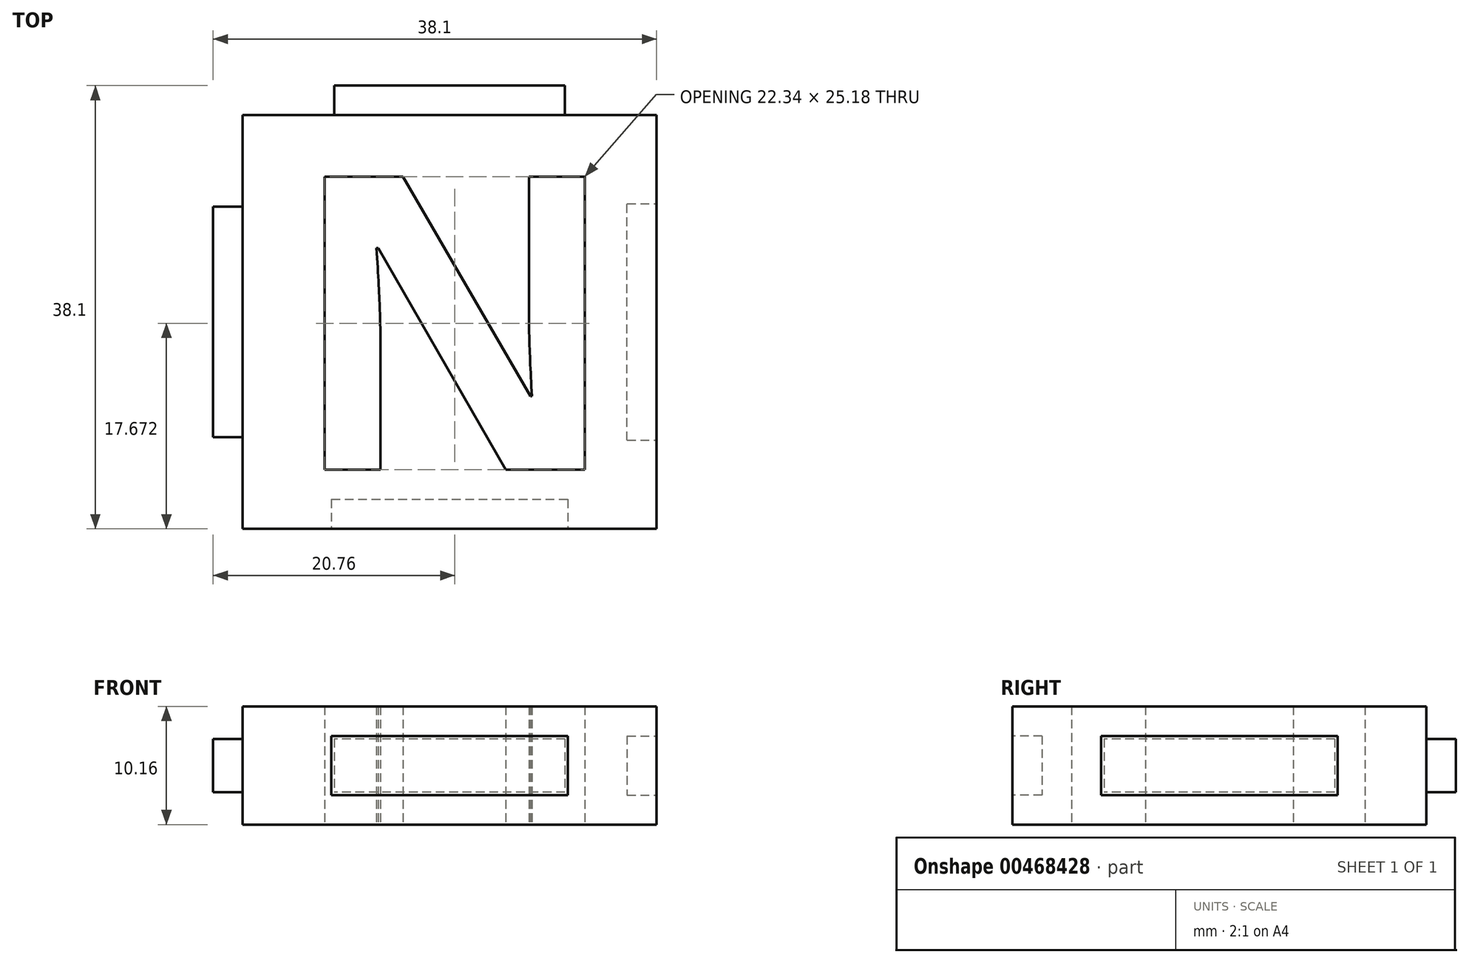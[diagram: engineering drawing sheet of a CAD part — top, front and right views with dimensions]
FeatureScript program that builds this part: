
annotation { "Feature Type Name" : "Feature", "Feature Type Description" : "" }
export const myFeature = defineFeature(function(context is Context, id is Id, definition is map)
    precondition{}
    {
        {
            var Q0;
            Q0=qCreatedBy(makeId("Top.planeOp"),FACE);
            var sketch = newSketch(context, id + "F0", { "sketchPlane" : qUnion([Q0])});
            skLineSegment(sketch, "E0.bottom", {"start": v(-17.78, 17.78) * mm, "end": v(17.78, 17.78) * mm});
            skLineSegment(sketch, "E0.top", {"start": v(-17.78, -17.78) * mm, "end": v(17.78, -17.78) * mm});
            skLineSegment(sketch, "E0.left", {"start": v(-17.78, 17.78) * mm, "end": v(-17.78, -17.78) * mm});
            skLineSegment(sketch, "E0.right", {"start": v(17.78, 17.78) * mm, "end": v(17.78, -17.78) * mm});
            skText(sketch, "E1", { "text": "N", "fontName": "OpenSans-Bold.ttf"});
            const initialGuessF0  = {"E1": [-0.0139, -0.0127, 1, 0, 0.0254]};
            skSetInitialGuess(sketch, initialGuessF0);
            skSolve(sketch);
        }
        {
            var Q0;
            Q0=qSketchRegion(id+"F0",true);
            extrude(context, id + "F1", {"entities" : qUnion([Q0]), "endBound" : BoundingType.SYMMETRIC, "depth" : 10.16 * mm});
        }
        {
            var Q0;
            Q0=makeQuery(id+"F1.opExtrude","SWEPT_FACE",FACE,{"disambiguationData":[OSD([sQuery(id+"F0.wireOp",EDGE,"E0.bottom")])]});
            var sketch = newSketch(context, id + "F2", { "sketchPlane" : qUnion([Q0])});
            skLineSegment(sketch, "E2.bottom", {"start": v(-9.9, 2.29) * mm, "end": v(9.9, 2.29) * mm});
            skLineSegment(sketch, "E2.top", {"start": v(-9.9, -2.29) * mm, "end": v(9.9, -2.29) * mm});
            skLineSegment(sketch, "E2.left", {"start": v(-9.9, 2.29) * mm, "end": v(-9.9, -2.29) * mm});
            skLineSegment(sketch, "E2.right", {"start": v(9.9, 2.29) * mm, "end": v(9.9, -2.29) * mm});
            skSolve(sketch);
        }
        {
            var Q0;
            Q0=qSketchRegion(id+"F2",true);
            extrude(context, id + "F3", {"entities" : qUnion([Q0]), "operationType" : NewBodyOperationType.ADD, "depth" : 2.54 * mm});
        }
        {
            var Q0;
            Q0=makeQuery(id+"F1.opExtrude","SWEPT_FACE",FACE,{"disambiguationData":[OSD([sQuery(id+"F0.wireOp",EDGE,"E0.left")])]});
            var sketch = newSketch(context, id + "F4", { "sketchPlane" : qUnion([Q0])});
            skLineSegment(sketch, "E3.bottom", {"start": v(-9.9, 2.29) * mm, "end": v(9.9, 2.29) * mm});
            skLineSegment(sketch, "E3.top", {"start": v(-9.9, -2.29) * mm, "end": v(9.9, -2.29) * mm});
            skLineSegment(sketch, "E3.left", {"start": v(-9.9, 2.29) * mm, "end": v(-9.9, -2.29) * mm});
            skLineSegment(sketch, "E3.right", {"start": v(9.9, 2.29) * mm, "end": v(9.9, -2.29) * mm});
            skSolve(sketch);
        }
        {
            var Q0;
            Q0=qSketchRegion(id+"F4",true);
            extrude(context, id + "F5", {"entities" : qUnion([Q0]), "operationType" : NewBodyOperationType.ADD, "depth" : 2.54 * mm});
        }
        {
            var Q0;
            Q0=makeQuery(id+"F1.opExtrude","SWEPT_FACE",FACE,{"disambiguationData":[OSD([sQuery(id+"F0.wireOp",EDGE,"E0.top")])]});
            var sketch = newSketch(context, id + "F6", { "sketchPlane" : qUnion([Q0])});
            skLineSegment(sketch, "E4.bottom", {"start": v(-10.16, 2.54) * mm, "end": v(10.16, 2.54) * mm});
            skLineSegment(sketch, "E4.top", {"start": v(-10.16, -2.54) * mm, "end": v(10.16, -2.54) * mm});
            skLineSegment(sketch, "E4.left", {"start": v(-10.16, 2.54) * mm, "end": v(-10.16, -2.54) * mm});
            skLineSegment(sketch, "E4.right", {"start": v(10.16, 2.54) * mm, "end": v(10.16, -2.54) * mm});
            skSolve(sketch);
        }
        {
            var Q0;
            Q0=qSketchRegion(id+"F6",true);
            extrude(context, id + "F7", {"entities" : qUnion([Q0]), "operationType" : NewBodyOperationType.REMOVE, "oppositeDirection" : true, "depth" : 2.54 * mm});
        }
        {
            var Q0;
            Q0=makeQuery(id+"F1.opExtrude","SWEPT_FACE",FACE,{"disambiguationData":[OSD([sQuery(id+"F0.wireOp",EDGE,"E0.right")])]});
            var sketch = newSketch(context, id + "F8", { "sketchPlane" : qUnion([Q0])});
            skLineSegment(sketch, "E5.bottom", {"start": v(-10.16, 2.54) * mm, "end": v(10.16, 2.54) * mm});
            skLineSegment(sketch, "E5.top", {"start": v(-10.16, -2.54) * mm, "end": v(10.16, -2.54) * mm});
            skLineSegment(sketch, "E5.left", {"start": v(-10.16, 2.54) * mm, "end": v(-10.16, -2.54) * mm});
            skLineSegment(sketch, "E5.right", {"start": v(10.16, 2.54) * mm, "end": v(10.16, -2.54) * mm});
            skSolve(sketch);
        }
        {
            var Q0;
            Q0=qSketchRegion(id+"F8",true);
            extrude(context, id + "F9", {"entities" : qUnion([Q0]), "operationType" : NewBodyOperationType.REMOVE, "oppositeDirection" : true, "depth" : 2.54 * mm});
        }
    });
